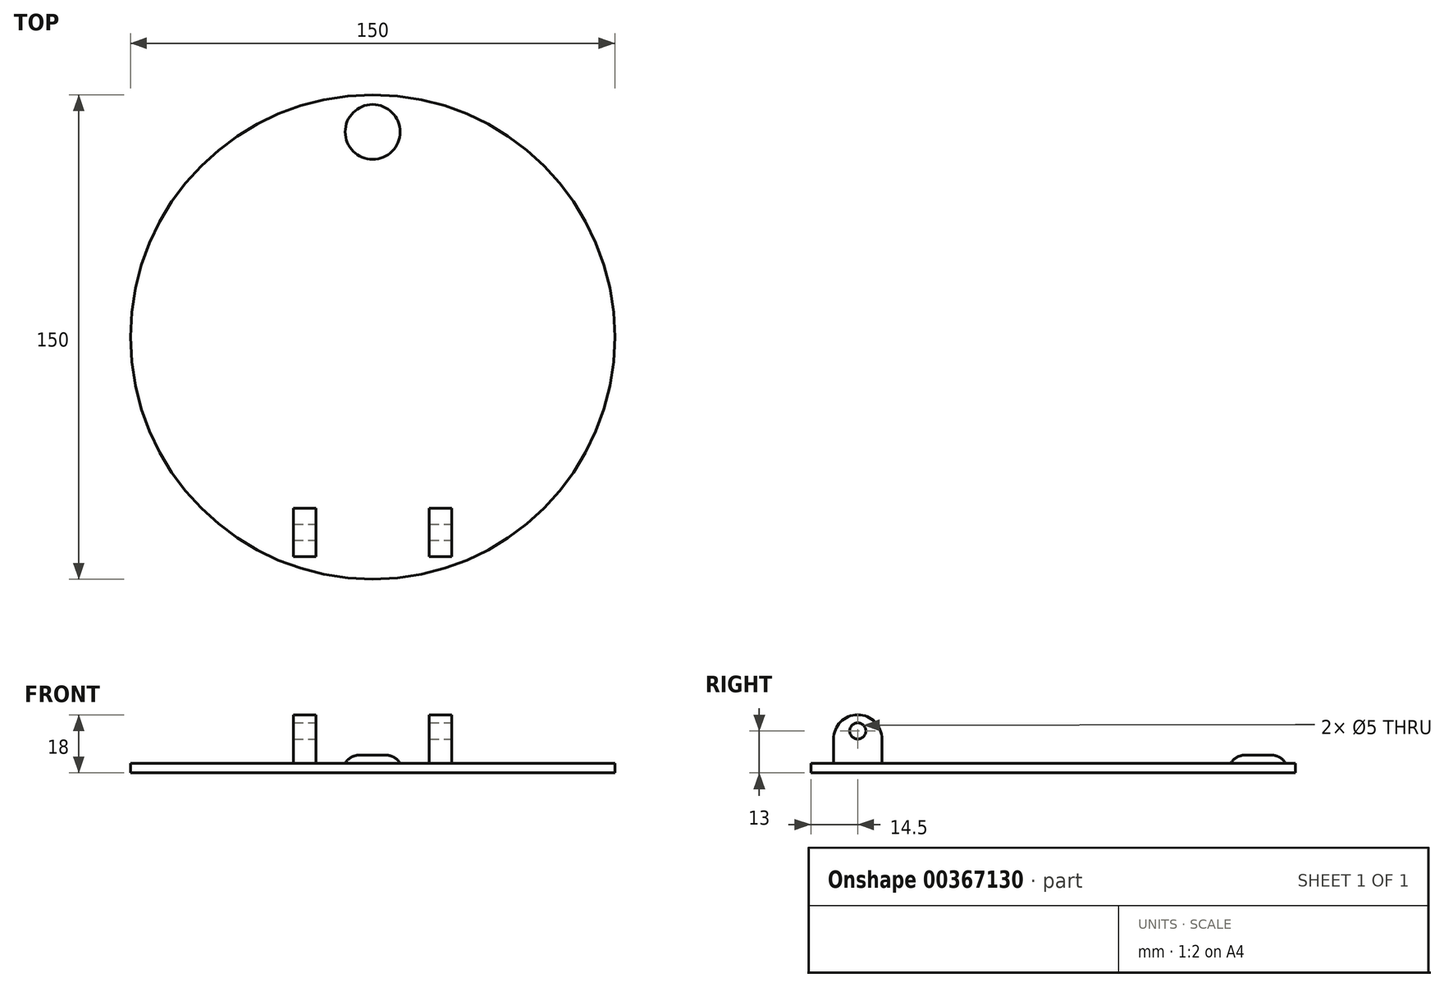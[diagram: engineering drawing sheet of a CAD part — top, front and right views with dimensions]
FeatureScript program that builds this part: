
annotation { "Feature Type Name" : "Feature", "Feature Type Description" : "" }
export const myFeature = defineFeature(function(context is Context, id is Id, definition is map)
    precondition{}
    {
        {
            var Q0;
            Q0=qCreatedBy(makeId("Top.planeOp"),FACE);
            var sketch = newSketch(context, id + "F0", { "sketchPlane" : qUnion([Q0])});
            skCircle(sketch, "E0.0", {"center": v(0, 0) * mm, "radius": 72 * mm, "construction": true});
            skCircle(sketch, "E1.0", {"center": v(0, 0) * mm, "radius": 53 * mm, "construction": true});
            skLineSegment(sketch, "E2.bottom", {"start": v(-23.66, -53) * mm, "end": v(23.66, -53) * mm, "construction": true});
            skLineSegment(sketch, "E2.top", {"start": v(-23.66, -68) * mm, "end": v(23.66, -68) * mm, "construction": true});
            skLineSegment(sketch, "E2.left", {"start": v(-23.66, -53) * mm, "end": v(-23.66, -68) * mm, "construction": true});
            skLineSegment(sketch, "E2.right", {"start": v(23.66, -53) * mm, "end": v(23.66, -68) * mm, "construction": true});
            skLineSegment(sketch, "E3", {"start": v(0, 18.12) * mm, "end": v(0, -52.12) * mm, "construction": true});
            skLineSegment(sketch, "E4", {"start": v(-16.16, -68) * mm, "end": v(-16.16, -53) * mm, "construction": true});
            skLineSegment(sketch, "E5", {"start": v(-16.16, -53) * mm, "end": v(16.16, -53) * mm, "construction": true});
            skLineSegment(sketch, "E6", {"start": v(16.16, -53) * mm, "end": v(16.16, -68) * mm, "construction": true});
            skLineSegment(sketch, "E7.bottom", {"start": v(-24.5, -53) * mm, "end": v(-17.5, -53) * mm});
            skLineSegment(sketch, "E7.top", {"start": v(-24.5, -68) * mm, "end": v(-17.5, -68) * mm});
            skLineSegment(sketch, "E7.left", {"start": v(-24.5, -53) * mm, "end": v(-24.5, -68) * mm});
            skLineSegment(sketch, "E7.right", {"start": v(-17.5, -53) * mm, "end": v(-17.5, -68) * mm});
            skLineSegment(sketch, "E8.bottom", {"start": v(24.5, -53) * mm, "end": v(17.5, -53) * mm});
            skLineSegment(sketch, "E8.top", {"start": v(24.5, -68) * mm, "end": v(17.5, -68) * mm});
            skLineSegment(sketch, "E8.left", {"start": v(24.5, -53) * mm, "end": v(24.5, -68) * mm});
            skLineSegment(sketch, "E8.right", {"start": v(17.5, -53) * mm, "end": v(17.5, -68) * mm});
            skCircle(sketch, "E9", {"center": v(0, 0) * mm, "radius": 75 * mm});
            skSolve(sketch);
        }
        {
            var Q0;
            Q0=makeQuery(id+"F0.imprint","IMPRINT",FACE,{"disambiguationData":[TD([[makeQuery(id+"F0.imprint","IMPRINT",EDGE,{"derivedFrom":sQuery(id+"F0.wireOp",EDGE,"E7.bottom")}),1.0]])]});
            var Q1;
            Q1=makeQuery(id+"F0.imprint","IMPRINT",FACE,{"disambiguationData":[TD([[makeQuery(id+"F0.imprint","IMPRINT",EDGE,{"derivedFrom":sQuery(id+"F0.wireOp",EDGE,"E7.bottom")}),-1.0]])]});
            var Q2;
            Q2=makeQuery(id+"F0.imprint","IMPRINT",FACE,{"disambiguationData":[TD([[makeQuery(id+"F0.imprint","IMPRINT",EDGE,{"derivedFrom":sQuery(id+"F0.wireOp",EDGE,"E8.bottom")}),1.0]])]});
            extrude(context, id + "F1", {"entities" : qUnion([Q0, Q1, Q2]), "oppositeDirection" : true, "depth" : 3 * mm, "offsetDistance" : 25 * mm});
        }
        {
            var Q0;
            Q0=makeQuery(id+"F0.imprint","IMPRINT",FACE,{"disambiguationData":[TD([[makeQuery(id+"F0.imprint","IMPRINT",EDGE,{"derivedFrom":sQuery(id+"F0.wireOp",EDGE,"E8.bottom")}),1.0]])]});
            var Q1;
            Q1=makeQuery(id+"F0.imprint","IMPRINT",FACE,{"disambiguationData":[TD([[makeQuery(id+"F0.imprint","IMPRINT",EDGE,{"derivedFrom":sQuery(id+"F0.wireOp",EDGE,"E7.bottom")}),-1.0]])]});
            extrude(context, id + "F2", {"entities" : qUnion([Q0, Q1]), "operationType" : NewBodyOperationType.ADD, "depth" : 15 * mm, "offsetDistance" : 25 * mm});
        }
        {
            var Q0;
            Q0=makeQuery(id+"F2.opExtrude","SWEPT_FACE",FACE,{"disambiguationData":[OSD([sQuery(id+"F0.wireOp",EDGE,"E8.left")])]});
            var sketch = newSketch(context, id + "F3", { "sketchPlane" : qUnion([Q0])});
            skCircle(sketch, "E10", {"center": v(-60.5, 10) * mm, "radius": 2.5 * mm});
            skLineSegment(sketch, "E11", {"start": v(-60.5, 10) * mm, "end": v(-53, 10) * mm, "construction": true});
            skLineSegment(sketch, "E12", {"start": v(-60.5, 10) * mm, "end": v(-68, 10) * mm, "construction": true});
            skPoint(sketch, "E12.endSnap0", {"position": v(-68, 7.5) * mm});
            skLineSegment(sketch, "E13", {"start": v(-60.5, 10) * mm, "end": v(-60.5, 12.5) * mm, "construction": true});
            skLineSegment(sketch, "E14", {"start": v(-60.5, 12.5) * mm, "end": v(-60.5, 15) * mm, "construction": true});
            skArc(sketch, "E15", {"start": v(-53, 7.5) * mm, "mid": v(-60.5, 15) * mm, "end": v(-68, 7.5) * mm});
            skSolve(sketch);
        }
        {
            var Q0;
            {var subQ0=sQuery(id+"F3.wireOp",EDGE,"E15");var subQ1=sQuery(id+"F0.wireOp",EDGE,"E8.left");var subQ4=makeQuery(id+"F2.opExtrude","CAP_EDGE",EDGE,{"disambiguationData":[OSD([subQ1])],"isStart":false});var subQ5=makeQuery(id+"F3.imprint","INTERSECT",VERTEX,{"derivedFrom":[subQ4,subQ0]});Q0=makeQuery(id+"F3.imprint","IMPRINT",FACE,{"disambiguationData":[TD([[makeQuery(id+"F3.imprint","IMPRINT",EDGE,{"disambiguationData":[TD([[subQ5,-1.0]])],"derivedFrom":subQ0}),-1.0]])]});}
            var Q1;
            {var subQ0=sQuery(id+"F3.wireOp",EDGE,"E15");var subQ1=sQuery(id+"F0.wireOp",EDGE,"E8.left");var subQ4=makeQuery(id+"F2.opExtrude","CAP_EDGE",EDGE,{"disambiguationData":[OSD([subQ1])],"isStart":false});var subQ5=makeQuery(id+"F3.imprint","INTERSECT",VERTEX,{"derivedFrom":[subQ4,subQ0]});Q1=makeQuery(id+"F3.imprint","IMPRINT",FACE,{"disambiguationData":[TD([[makeQuery(id+"F3.imprint","IMPRINT",EDGE,{"disambiguationData":[TD([[subQ5,1.0]])],"derivedFrom":subQ0}),-1.0]])]});}
            var Q2;
            Q2=makeQuery(id+"F3.imprint","IMPRINT",FACE,{"disambiguationData":[TD([[makeQuery(id+"F3.imprint","IMPRINT",EDGE,{"derivedFrom":sQuery(id+"F3.wireOp",EDGE,"E10")}),1.0]])]});
            extrude(context, id + "F4", {"entities" : qUnion([Q0, Q1, Q2]), "operationType" : NewBodyOperationType.REMOVE, "endBound" : BoundingType.THROUGH_ALL, "oppositeDirection" : true, "depth" : 25 * mm, "offsetDistance" : 25 * mm});
        }
        {
            var Q0;
            Q0=makeQuery(id+"F0.imprint","IMPRINT",FACE,{"disambiguationData":[TD([[makeQuery(id+"F0.imprint","IMPRINT",EDGE,{"derivedFrom":sQuery(id+"F0.wireOp",EDGE,"E7.bottom")}),1.0]])]});
            var sketch = newSketch(context, id + "F5", { "sketchPlane" : qUnion([Q0])});
            skCircle(sketch, "E16", {"center": v(0, 63.5) * mm, "radius": 8.5 * mm});
            skSolve(sketch);
        }
        {
            var Q0;
            Q0=makeQuery(id+"F5.imprint","IMPRINT",FACE,{"disambiguationData":[TD([[makeQuery(id+"F5.imprint","IMPRINT",EDGE,{"derivedFrom":sQuery(id+"F5.wireOp",EDGE,"E16")}),1.0]])]});
            extrude(context, id + "F6", {"entities" : qUnion([Q0]), "operationType" : NewBodyOperationType.ADD, "depth" : 2.5 * mm, "offsetDistance" : 25 * mm, "hasDraft" : true, "draftAngle" : 10 * degree, "draftPullDirection" : true});
        }
        {
            var Q0;
            Q0=makeQuery(id+"F6.opExtrude","CAP_EDGE",EDGE,{"disambiguationData":[OSD([sQuery(id+"F5.wireOp",EDGE,"E16")])],"isStart":false});
            fillet(context, id + "F7", {"entities" : qUnion([Q0]), "radius" : 5 * mm, "tangentPropagation" : true, "allowEdgeOverflow" : false});
        }
    });
